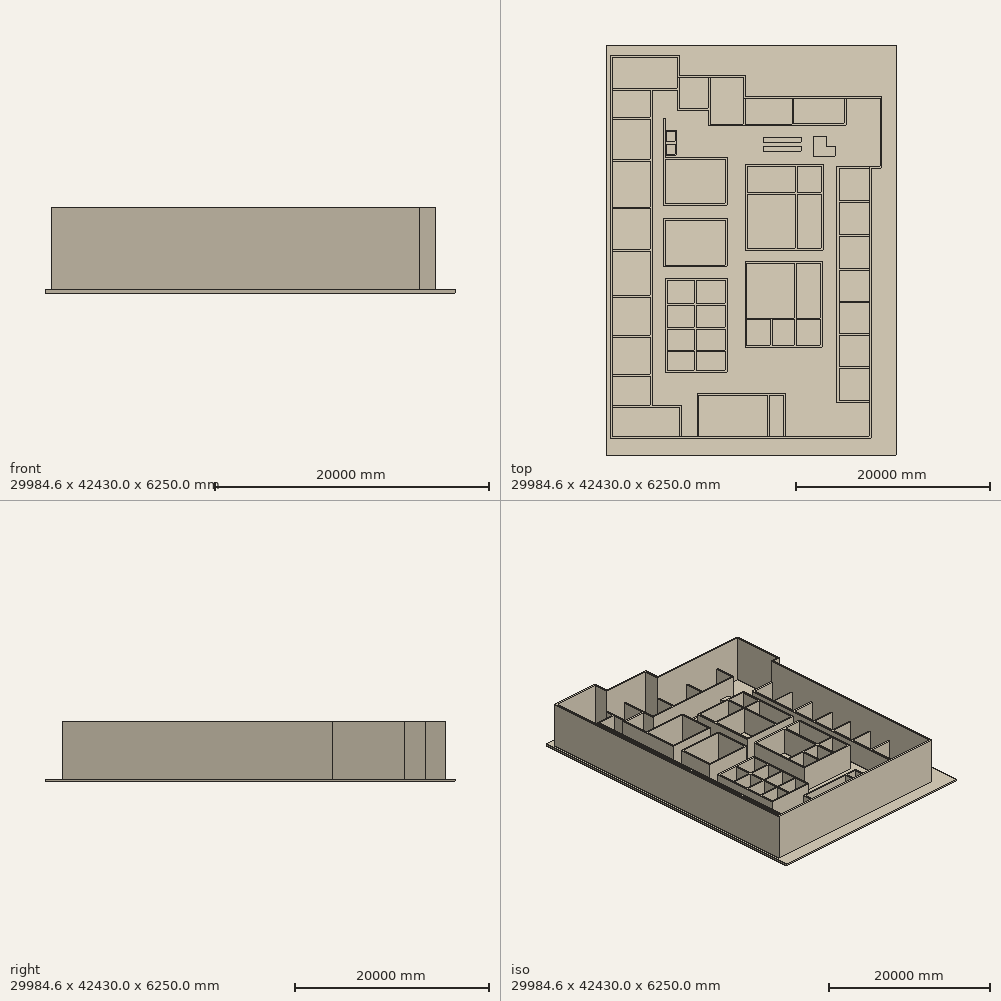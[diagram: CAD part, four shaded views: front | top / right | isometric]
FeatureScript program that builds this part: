
annotation { "Feature Type Name" : "Feature", "Feature Type Description" : "" }
export const myFeature = defineFeature(function(context is Context, id is Id, definition is map)
    precondition{}
    {
        {
            var Q0;
            Q0=qCreatedBy(makeId("Top.planeOp"),FACE);
            var sketch = newSketch(context, id + "F0", { "sketchPlane" : qUnion([Q0])});
            skLineSegment(sketch, "E0", {"start": v(414.42, 1769.53) * mm, "end": v(27384.85, 1769.53) * mm});
            skLineSegment(sketch, "E1", {"start": v(27384.85, 1769.53) * mm, "end": v(27384.85, 29713.26) * mm});
            skLineSegment(sketch, "E2", {"start": v(27384.85, 29713.26) * mm, "end": v(28491.53, 29713.26) * mm});
            skLineSegment(sketch, "E3", {"start": v(28491.53, 29713.26) * mm, "end": v(28491.53, 37144.84) * mm});
            skLineSegment(sketch, "E4", {"start": v(28491.53, 37144.84) * mm, "end": v(14379.1, 37144.84) * mm});
            skLineSegment(sketch, "E5", {"start": v(14379.1, 37144.84) * mm, "end": v(14379.1, 39309.76) * mm});
            skLineSegment(sketch, "E6", {"start": v(14379.1, 39309.76) * mm, "end": v(7514.71, 39309.76) * mm});
            skLineSegment(sketch, "E7", {"start": v(7514.71, 39309.76) * mm, "end": v(7514.71, 41362.76) * mm});
            skLineSegment(sketch, "E8", {"start": v(7514.71, 41362.76) * mm, "end": v(414.42, 41362.76) * mm});
            skLineSegment(sketch, "E9", {"start": v(414.42, 41362.76) * mm, "end": v(414.42, 1769.53) * mm});
            skLineSegment(sketch, "E10", {"start": v(614.42, 1969.53) * mm, "end": v(27184.85, 1969.53) * mm});
            skLineSegment(sketch, "E11", {"start": v(27184.85, 1969.53) * mm, "end": v(27184.85, 29913.26) * mm});
            skLineSegment(sketch, "E12", {"start": v(27184.85, 29913.26) * mm, "end": v(28291.53, 29913.26) * mm});
            skLineSegment(sketch, "E13", {"start": v(28291.53, 29913.26) * mm, "end": v(28291.53, 36944.84) * mm});
            skLineSegment(sketch, "E14", {"start": v(28291.53, 36944.84) * mm, "end": v(14179.1, 36944.84) * mm});
            skLineSegment(sketch, "E15", {"start": v(14179.1, 36944.84) * mm, "end": v(14179.1, 39109.76) * mm});
            skLineSegment(sketch, "E16", {"start": v(14179.1, 39109.76) * mm, "end": v(7314.71, 39109.76) * mm});
            skLineSegment(sketch, "E17", {"start": v(7314.71, 39109.76) * mm, "end": v(7314.71, 41162.76) * mm});
            skLineSegment(sketch, "E18", {"start": v(7314.71, 41162.76) * mm, "end": v(614.42, 41162.76) * mm});
            skLineSegment(sketch, "E19", {"start": v(614.42, 41162.76) * mm, "end": v(614.42, 1969.53) * mm});
            skSolve(sketch);
        }
        {
            var Q0;
            Q0=makeQuery(id+"F0.imprint","IMPRINT",FACE,{"disambiguationData":[TD([[makeQuery(id+"F0.imprint","IMPRINT",EDGE,{"derivedFrom":sQuery(id+"F0.wireOp",EDGE,"E0")}),1.0]])]});
            extrude(context, id + "F1", {"entities" : qUnion([Q0]), "depth" : 6000 * mm, "offsetDistance" : 25 * mm});
        }
        {
            var Q0;
            Q0=qCreatedBy(makeId("Top.planeOp"),FACE);
            var sketch = newSketch(context, id + "F2", { "sketchPlane" : qUnion([Q0])});
            skLineSegment(sketch, "E20.bottom", {"start": v(18534.6, 6431.3) * mm, "end": v(9367.4, 6431.3) * mm});
            skLineSegment(sketch, "E20.top", {"start": v(18534.6, 1969.52) * mm, "end": v(9367.4, 1969.52) * mm});
            skLineSegment(sketch, "E20.left", {"start": v(18534.6, 6431.3) * mm, "end": v(18534.6, 1969.52) * mm});
            skLineSegment(sketch, "E20.right", {"start": v(9367.4, 6431.3) * mm, "end": v(9367.4, 1969.52) * mm});
            skLineSegment(sketch, "E21.bottom", {"start": v(9542.41, 6224.02) * mm, "end": v(16684.38, 6224.02) * mm});
            skLineSegment(sketch, "E21.top", {"start": v(9542.41, 1969.52) * mm, "end": v(16684.38, 1969.52) * mm});
            skLineSegment(sketch, "E21.left", {"start": v(9542.41, 6224.02) * mm, "end": v(9542.41, 1969.52) * mm});
            skLineSegment(sketch, "E21.right", {"start": v(16684.38, 6224.02) * mm, "end": v(16684.38, 1969.52) * mm});
            skLineSegment(sketch, "E22.bottom", {"start": v(16877.72, 6224.02) * mm, "end": v(18340.36, 6224.02) * mm});
            skLineSegment(sketch, "E22.top", {"start": v(16877.72, 1969.52) * mm, "end": v(18340.36, 1969.52) * mm});
            skLineSegment(sketch, "E22.left", {"start": v(16877.72, 6224.02) * mm, "end": v(16877.72, 1969.52) * mm});
            skLineSegment(sketch, "E22.right", {"start": v(18340.36, 6224.02) * mm, "end": v(18340.36, 1969.52) * mm});
            skSolve(sketch);
        }
        {
            var Q0;
            Q0=makeQuery(id+"F2.imprint","IMPRINT",FACE,{"disambiguationData":[TD([[makeQuery(id+"F2.imprint","IMPRINT",EDGE,{"derivedFrom":sQuery(id+"F2.wireOp",EDGE,"E20.bottom")}),1.0]])]});
            extrude(context, id + "F3", {"entities" : qUnion([Q0]), "depth" : 3500 * mm, "offsetDistance" : 25 * mm});
        }
        {
            var Q0;
            Q0=qCreatedBy(makeId("Top.planeOp"),FACE);
            var sketch = newSketch(context, id + "F4", { "sketchPlane" : qUnion([Q0])});
            skLineSegment(sketch, "E23.bottom", {"start": v(7784.5, 1967.61) * mm, "end": v(609.72, 1967.61) * mm});
            skLineSegment(sketch, "E23.top", {"start": v(7784.5, 5141.6) * mm, "end": v(609.72, 5141.6) * mm});
            skLineSegment(sketch, "E23.left", {"start": v(7784.5, 1967.61) * mm, "end": v(7784.5, 5141.6) * mm});
            skLineSegment(sketch, "E23.right", {"start": v(609.72, 1967.61) * mm, "end": v(609.72, 5141.6) * mm});
            skLineSegment(sketch, "E24.bottom", {"start": v(609.72, 4967.2) * mm, "end": v(7570.65, 4967.2) * mm});
            skLineSegment(sketch, "E24.top", {"start": v(609.72, 1967.61) * mm, "end": v(7570.65, 1967.61) * mm});
            skLineSegment(sketch, "E24.left", {"start": v(609.72, 4967.2) * mm, "end": v(609.72, 1967.61) * mm});
            skLineSegment(sketch, "E24.right", {"start": v(7570.65, 4967.2) * mm, "end": v(7570.65, 1967.61) * mm});
            skLineSegment(sketch, "E25.bottom", {"start": v(4738.63, 5141.6) * mm, "end": v(609.72, 5141.6) * mm});
            skLineSegment(sketch, "E25.top", {"start": v(4738.63, 8338.8) * mm, "end": v(609.72, 8338.8) * mm});
            skLineSegment(sketch, "E25.left", {"start": v(4738.63, 5141.6) * mm, "end": v(4738.63, 8338.8) * mm});
            skLineSegment(sketch, "E25.right", {"start": v(609.72, 5141.6) * mm, "end": v(609.72, 8338.8) * mm});
            skLineSegment(sketch, "E26.bottom", {"start": v(609.72, 8160.97) * mm, "end": v(4559, 8160.97) * mm});
            skLineSegment(sketch, "E26.top", {"start": v(609.72, 5141.6) * mm, "end": v(4559, 5141.6) * mm});
            skLineSegment(sketch, "E26.left", {"start": v(609.72, 8160.97) * mm, "end": v(609.72, 5141.6) * mm});
            skLineSegment(sketch, "E26.right", {"start": v(4559, 8160.97) * mm, "end": v(4559, 5141.6) * mm});
            skLineSegment(sketch, "E27.top", {"start": v(4738.63, 12384.25) * mm, "end": v(609.72, 12384.25) * mm});
            skLineSegment(sketch, "E27.left", {"start": v(4738.63, 8338.8) * mm, "end": v(4738.63, 12384.25) * mm});
            skLineSegment(sketch, "E27.right", {"start": v(609.72, 8338.8) * mm, "end": v(609.72, 12384.25) * mm});
            skLineSegment(sketch, "E28.bottom", {"start": v(609.72, 12225.64) * mm, "end": v(4559, 12225.64) * mm});
            skLineSegment(sketch, "E28.top", {"start": v(609.72, 8338.8) * mm, "end": v(4559, 8338.8) * mm});
            skLineSegment(sketch, "E28.left", {"start": v(609.72, 12225.64) * mm, "end": v(609.72, 8338.8) * mm});
            skLineSegment(sketch, "E28.right", {"start": v(4559, 12225.64) * mm, "end": v(4559, 8338.8) * mm});
            skLineSegment(sketch, "E29.top", {"start": v(4738.63, 16526.3) * mm, "end": v(609.72, 16526.3) * mm});
            skLineSegment(sketch, "E29.left", {"start": v(4738.63, 12384.25) * mm, "end": v(4738.63, 16526.3) * mm});
            skLineSegment(sketch, "E29.right", {"start": v(609.72, 12384.25) * mm, "end": v(609.72, 16526.3) * mm});
            skLineSegment(sketch, "E30.bottom", {"start": v(609.72, 16367) * mm, "end": v(4559, 16367) * mm});
            skLineSegment(sketch, "E30.top", {"start": v(609.72, 12384.25) * mm, "end": v(4559, 12384.25) * mm});
            skLineSegment(sketch, "E30.left", {"start": v(609.72, 16367) * mm, "end": v(609.72, 12384.25) * mm});
            skLineSegment(sketch, "E30.right", {"start": v(4559, 16367) * mm, "end": v(4559, 12384.25) * mm});
            skLineSegment(sketch, "E31.top", {"start": v(4738.63, 21320.6) * mm, "end": v(609.72, 21320.6) * mm});
            skLineSegment(sketch, "E31.left", {"start": v(4738.63, 16526.3) * mm, "end": v(4738.63, 21320.6) * mm});
            skLineSegment(sketch, "E31.right", {"start": v(609.72, 16526.3) * mm, "end": v(609.72, 21320.6) * mm});
            skLineSegment(sketch, "E32.bottom", {"start": v(609.72, 21131.98) * mm, "end": v(4559, 21131.98) * mm});
            skLineSegment(sketch, "E32.top", {"start": v(609.72, 16526.3) * mm, "end": v(4559, 16526.3) * mm});
            skLineSegment(sketch, "E32.left", {"start": v(609.72, 21131.98) * mm, "end": v(609.72, 16526.3) * mm});
            skLineSegment(sketch, "E32.right", {"start": v(4559, 21131.98) * mm, "end": v(4559, 16526.3) * mm});
            skLineSegment(sketch, "E33.top", {"start": v(4738.63, 25696.66) * mm, "end": v(609.72, 25696.66) * mm});
            skLineSegment(sketch, "E33.left", {"start": v(4738.63, 21320.6) * mm, "end": v(4738.63, 25696.66) * mm});
            skLineSegment(sketch, "E33.right", {"start": v(609.72, 21320.6) * mm, "end": v(609.72, 25696.66) * mm});
            skLineSegment(sketch, "E34.bottom", {"start": v(609.72, 25533.64) * mm, "end": v(4559, 25533.64) * mm});
            skLineSegment(sketch, "E34.top", {"start": v(609.72, 21320.6) * mm, "end": v(4559, 21320.6) * mm});
            skLineSegment(sketch, "E34.left", {"start": v(609.72, 25533.64) * mm, "end": v(609.72, 21320.6) * mm});
            skLineSegment(sketch, "E34.right", {"start": v(4559, 25533.64) * mm, "end": v(4559, 21320.6) * mm});
            skLineSegment(sketch, "E35.top", {"start": v(4738.63, 30588.27) * mm, "end": v(609.72, 30588.27) * mm});
            skLineSegment(sketch, "E35.left", {"start": v(4738.63, 25696.66) * mm, "end": v(4738.63, 30588.27) * mm});
            skLineSegment(sketch, "E35.right", {"start": v(609.72, 25696.66) * mm, "end": v(609.72, 30588.27) * mm});
            skLineSegment(sketch, "E36.bottom", {"start": v(609.72, 30407.33) * mm, "end": v(4559, 30407.33) * mm});
            skLineSegment(sketch, "E36.top", {"start": v(609.72, 25696.66) * mm, "end": v(4559, 25696.66) * mm});
            skLineSegment(sketch, "E36.left", {"start": v(609.72, 30407.33) * mm, "end": v(609.72, 25696.66) * mm});
            skLineSegment(sketch, "E36.right", {"start": v(4559, 30407.33) * mm, "end": v(4559, 25696.66) * mm});
            skLineSegment(sketch, "E37.top", {"start": v(4738.63, 34934.96) * mm, "end": v(609.72, 34934.96) * mm});
            skLineSegment(sketch, "E37.left", {"start": v(4738.63, 30588.27) * mm, "end": v(4738.63, 34934.96) * mm});
            skLineSegment(sketch, "E37.right", {"start": v(609.72, 30588.27) * mm, "end": v(609.72, 34934.96) * mm});
            skLineSegment(sketch, "E38.bottom", {"start": v(609.72, 34776.35) * mm, "end": v(4559, 34776.35) * mm});
            skLineSegment(sketch, "E38.top", {"start": v(609.72, 30588.27) * mm, "end": v(4559, 30588.27) * mm});
            skLineSegment(sketch, "E38.left", {"start": v(609.72, 34776.35) * mm, "end": v(609.72, 30588.27) * mm});
            skLineSegment(sketch, "E38.right", {"start": v(4559, 34776.35) * mm, "end": v(4559, 30588.27) * mm});
            skLineSegment(sketch, "E39.top", {"start": v(4738.63, 37981.85) * mm, "end": v(609.72, 37981.85) * mm});
            skLineSegment(sketch, "E39.left", {"start": v(4738.63, 34934.96) * mm, "end": v(4738.63, 37981.85) * mm});
            skLineSegment(sketch, "E39.right", {"start": v(609.72, 34934.96) * mm, "end": v(609.72, 37981.85) * mm});
            skLineSegment(sketch, "E40.bottom", {"start": v(609.72, 37824.67) * mm, "end": v(4559, 37824.67) * mm});
            skLineSegment(sketch, "E40.top", {"start": v(609.72, 34934.96) * mm, "end": v(4559, 34934.96) * mm});
            skLineSegment(sketch, "E40.left", {"start": v(609.72, 37824.67) * mm, "end": v(609.72, 34934.96) * mm});
            skLineSegment(sketch, "E40.right", {"start": v(4559, 37824.67) * mm, "end": v(4559, 34934.96) * mm});
            skSolve(sketch);
        }
        {
            var Q0;
            {var subQ3=sQuery(id+"F4.wireOp",EDGE,"E23.left");Q0=makeQuery(id+"F4.imprint","IMPRINT",FACE,{"disambiguationData":[TD([[makeQuery(id+"F4.imprint","IMPRINT",EDGE,{"derivedFrom":subQ3}),1.0]])]});}
            var Q1;
            {var subQ0=sQuery(id+"F4.wireOp",EDGE,"E25.left");Q1=makeQuery(id+"F4.imprint","IMPRINT",FACE,{"disambiguationData":[TD([[makeQuery(id+"F4.imprint","IMPRINT",EDGE,{"derivedFrom":subQ0}),1.0]])]});}
            var Q2;
            {var subQ0=sQuery(id+"F4.wireOp",EDGE,"E27.left");Q2=makeQuery(id+"F4.imprint","IMPRINT",FACE,{"disambiguationData":[TD([[makeQuery(id+"F4.imprint","IMPRINT",EDGE,{"derivedFrom":subQ0}),1.0]])]});}
            var Q3;
            {var subQ0=sQuery(id+"F4.wireOp",EDGE,"E29.left");Q3=makeQuery(id+"F4.imprint","IMPRINT",FACE,{"disambiguationData":[TD([[makeQuery(id+"F4.imprint","IMPRINT",EDGE,{"derivedFrom":subQ0}),1.0]])]});}
            var Q4;
            {var subQ0=sQuery(id+"F4.wireOp",EDGE,"E31.left");Q4=makeQuery(id+"F4.imprint","IMPRINT",FACE,{"disambiguationData":[TD([[makeQuery(id+"F4.imprint","IMPRINT",EDGE,{"derivedFrom":subQ0}),1.0]])]});}
            var Q5;
            {var subQ0=sQuery(id+"F4.wireOp",EDGE,"E33.left");Q5=makeQuery(id+"F4.imprint","IMPRINT",FACE,{"disambiguationData":[TD([[makeQuery(id+"F4.imprint","IMPRINT",EDGE,{"derivedFrom":subQ0}),1.0]])]});}
            var Q6;
            {var subQ0=sQuery(id+"F4.wireOp",EDGE,"E35.left");Q6=makeQuery(id+"F4.imprint","IMPRINT",FACE,{"disambiguationData":[TD([[makeQuery(id+"F4.imprint","IMPRINT",EDGE,{"derivedFrom":subQ0}),1.0]])]});}
            var Q7;
            {var subQ0=sQuery(id+"F4.wireOp",EDGE,"E37.left");Q7=makeQuery(id+"F4.imprint","IMPRINT",FACE,{"disambiguationData":[TD([[makeQuery(id+"F4.imprint","IMPRINT",EDGE,{"derivedFrom":subQ0}),1.0]])]});}
            var Q8;
            {var subQ1=sQuery(id+"F4.wireOp",EDGE,"E39.top");Q8=makeQuery(id+"F4.imprint","IMPRINT",FACE,{"disambiguationData":[TD([[makeQuery(id+"F4.imprint","IMPRINT",EDGE,{"derivedFrom":subQ1}),1.0]])]});}
            extrude(context, id + "F5", {"entities" : qUnion([Q0, Q1, Q2, Q3, Q4, Q5, Q6, Q7, Q8]), "depth" : 3000 * mm, "offsetDistance" : 25 * mm});
        }
        {
            var Q0;
            Q0=qCreatedBy(makeId("Top.planeOp"),FACE);
            var sketch = newSketch(context, id + "F6", { "sketchPlane" : qUnion([Q0])});
            skLineSegment(sketch, "E41.bottom", {"start": v(24779.92, 36969.18) * mm, "end": v(19212.86, 36969.18) * mm});
            skLineSegment(sketch, "E41.top", {"start": v(24779.92, 34117.8) * mm, "end": v(19212.86, 34117.8) * mm});
            skLineSegment(sketch, "E41.left", {"start": v(24779.92, 36969.18) * mm, "end": v(24779.92, 34117.8) * mm});
            skLineSegment(sketch, "E41.right", {"start": v(19212.86, 36969.18) * mm, "end": v(19212.86, 34117.8) * mm});
            skLineSegment(sketch, "E42.bottom", {"start": v(19389.23, 34324.37) * mm, "end": v(24610.44, 34324.37) * mm});
            skLineSegment(sketch, "E42.top", {"start": v(19389.23, 36969.18) * mm, "end": v(24610.44, 36969.18) * mm});
            skLineSegment(sketch, "E42.left", {"start": v(19389.23, 34324.37) * mm, "end": v(19389.23, 36969.18) * mm});
            skLineSegment(sketch, "E42.right", {"start": v(24610.44, 34324.37) * mm, "end": v(24610.44, 36969.18) * mm});
            skLineSegment(sketch, "E43", {"start": v(19212.86, 36969.18) * mm, "end": v(13851.37, 36969.18) * mm, "construction": true});
            skLineSegment(sketch, "E44", {"start": v(14179.1, 36969.18) * mm, "end": v(14179.1, 34117.8) * mm, "construction": true});
            skLineSegment(sketch, "E45.bottom", {"start": v(14179.1, 36969.18) * mm, "end": v(19212.86, 36969.18) * mm});
            skLineSegment(sketch, "E45.top", {"start": v(14179.1, 34117.8) * mm, "end": v(19212.86, 34117.8) * mm});
            skLineSegment(sketch, "E45.left", {"start": v(14179.1, 36969.18) * mm, "end": v(14179.1, 34117.8) * mm});
            skLineSegment(sketch, "E46.bottom", {"start": v(19212.86, 34295.57) * mm, "end": v(14365.95, 34295.57) * mm});
            skLineSegment(sketch, "E46.top", {"start": v(19212.86, 36969.18) * mm, "end": v(14365.95, 36969.18) * mm});
            skLineSegment(sketch, "E46.left", {"start": v(19212.86, 34295.57) * mm, "end": v(19212.86, 36969.18) * mm});
            skLineSegment(sketch, "E46.right", {"start": v(14365.95, 34295.57) * mm, "end": v(14365.95, 36969.18) * mm});
            skLineSegment(sketch, "E47.bottom", {"start": v(14179.1, 34117.8) * mm, "end": v(10513.24, 34117.8) * mm});
            skLineSegment(sketch, "E47.top", {"start": v(14179.1, 39118.15) * mm, "end": v(10513.24, 39118.15) * mm});
            skLineSegment(sketch, "E47.left", {"start": v(14179.1, 34117.8) * mm, "end": v(14179.1, 39118.15) * mm});
            skLineSegment(sketch, "E47.right", {"start": v(10513.24, 34117.8) * mm, "end": v(10513.24, 39118.15) * mm});
            skLineSegment(sketch, "E48.bottom", {"start": v(14179.1, 34295.57) * mm, "end": v(10708.2, 34295.57) * mm});
            skLineSegment(sketch, "E48.top", {"start": v(14179.1, 39118.15) * mm, "end": v(10708.2, 39118.15) * mm});
            skLineSegment(sketch, "E48.left", {"start": v(14179.1, 34295.57) * mm, "end": v(14179.1, 39118.15) * mm});
            skLineSegment(sketch, "E48.right", {"start": v(10708.2, 34295.57) * mm, "end": v(10708.2, 39118.15) * mm});
            skLineSegment(sketch, "E49.bottom", {"start": v(10513.24, 35728.09) * mm, "end": v(7321.54, 35728.09) * mm});
            skLineSegment(sketch, "E49.top", {"start": v(10513.24, 39118.15) * mm, "end": v(7321.54, 39118.15) * mm});
            skLineSegment(sketch, "E49.left", {"start": v(10513.24, 35728.09) * mm, "end": v(10513.24, 39118.15) * mm});
            skLineSegment(sketch, "E49.right", {"start": v(7321.54, 35728.09) * mm, "end": v(7321.54, 39118.15) * mm});
            skLineSegment(sketch, "E50.bottom", {"start": v(10513.24, 35943.79) * mm, "end": v(7494.73, 35943.79) * mm});
            skLineSegment(sketch, "E50.top", {"start": v(10513.24, 39118.15) * mm, "end": v(7494.73, 39118.15) * mm});
            skLineSegment(sketch, "E50.left", {"start": v(10513.24, 35943.79) * mm, "end": v(10513.24, 39118.15) * mm});
            skLineSegment(sketch, "E50.right", {"start": v(7494.73, 35943.79) * mm, "end": v(7494.73, 39118.15) * mm});
            skLineSegment(sketch, "E51.bottom", {"start": v(4723.43, 37978.8) * mm, "end": v(7321.54, 37978.8) * mm});
            skLineSegment(sketch, "E51.top", {"start": v(4723.43, 37815.59) * mm, "end": v(7321.54, 37815.59) * mm});
            skLineSegment(sketch, "E51.left", {"start": v(4723.43, 37978.8) * mm, "end": v(4723.43, 37815.59) * mm});
            skLineSegment(sketch, "E51.right", {"start": v(7321.54, 37978.8) * mm, "end": v(7321.54, 37815.59) * mm});
            skSolve(sketch);
        }
        {
            var Q0;
            {var subQ0=sQuery(id+"F6.wireOp",EDGE,"E51.bottom");Q0=makeQuery(id+"F6.imprint","IMPRINT",FACE,{"disambiguationData":[TD([[makeQuery(id+"F6.imprint","IMPRINT",EDGE,{"derivedFrom":subQ0}),-1.0]])]});}
            var Q1;
            {var subQ1=sQuery(id+"F6.wireOp",EDGE,"E49.bottom");Q1=makeQuery(id+"F6.imprint","IMPRINT",FACE,{"disambiguationData":[TD([[makeQuery(id+"F6.imprint","IMPRINT",EDGE,{"derivedFrom":subQ1}),-1.0]])]});}
            var Q2;
            {var subQ4=sQuery(id+"F6.wireOp",EDGE,"E47.bottom");Q2=makeQuery(id+"F6.imprint","IMPRINT",FACE,{"disambiguationData":[TD([[makeQuery(id+"F6.imprint","IMPRINT",EDGE,{"derivedFrom":subQ4}),-1.0]])]});}
            var Q3;
            {var subQ4=sQuery(id+"F6.wireOp",EDGE,"E45.top");Q3=makeQuery(id+"F6.imprint","IMPRINT",FACE,{"disambiguationData":[TD([[makeQuery(id+"F6.imprint","IMPRINT",EDGE,{"derivedFrom":subQ4}),1.0]])]});}
            var Q4;
            {var subQ1=sQuery(id+"F6.wireOp",EDGE,"E41.top");Q4=makeQuery(id+"F6.imprint","IMPRINT",FACE,{"disambiguationData":[TD([[makeQuery(id+"F6.imprint","IMPRINT",EDGE,{"derivedFrom":subQ1}),-1.0]])]});}
            extrude(context, id + "F7", {"entities" : qUnion([Q0, Q1, Q2, Q3, Q4]), "depth" : 3000 * mm, "offsetDistance" : 25 * mm});
        }
        {
            var Q0;
            Q0=qCreatedBy(makeId("Top.planeOp"),FACE);
            var sketch = newSketch(context, id + "F8", { "sketchPlane" : qUnion([Q0])});
            skLineSegment(sketch, "E52.bottom", {"start": v(27206.14, 5463.2) * mm, "end": v(23827.33, 5463.2) * mm});
            skLineSegment(sketch, "E52.top", {"start": v(27206.14, 29937.1) * mm, "end": v(23827.33, 29937.1) * mm});
            skLineSegment(sketch, "E52.left", {"start": v(27206.14, 5463.2) * mm, "end": v(27206.14, 29937.1) * mm});
            skLineSegment(sketch, "E52.right", {"start": v(23827.33, 5463.2) * mm, "end": v(23827.33, 29937.1) * mm});
            skLineSegment(sketch, "E53.bottom", {"start": v(24058.5, 29721.69) * mm, "end": v(27206.14, 29721.69) * mm});
            skLineSegment(sketch, "E53.top", {"start": v(24058.5, 26383.7) * mm, "end": v(27206.14, 26383.7) * mm});
            skLineSegment(sketch, "E53.left", {"start": v(24058.5, 29721.69) * mm, "end": v(24058.5, 26383.7) * mm});
            skLineSegment(sketch, "E53.right", {"start": v(27206.14, 29721.69) * mm, "end": v(27206.14, 26383.7) * mm});
            skLineSegment(sketch, "E54.bottom", {"start": v(24058.5, 26211.66) * mm, "end": v(27206.14, 26211.66) * mm});
            skLineSegment(sketch, "E54.top", {"start": v(24058.5, 22860.98) * mm, "end": v(27206.14, 22860.98) * mm});
            skLineSegment(sketch, "E54.left", {"start": v(24058.5, 26211.66) * mm, "end": v(24058.5, 22860.98) * mm});
            skLineSegment(sketch, "E54.right", {"start": v(27206.14, 26211.66) * mm, "end": v(27206.14, 22860.98) * mm});
            skLineSegment(sketch, "E55.bottom", {"start": v(24058.5, 22674.67) * mm, "end": v(27206.14, 22674.67) * mm});
            skLineSegment(sketch, "E55.top", {"start": v(24058.5, 19320.51) * mm, "end": v(27206.14, 19320.51) * mm});
            skLineSegment(sketch, "E55.left", {"start": v(24058.5, 22674.67) * mm, "end": v(24058.5, 19320.51) * mm});
            skLineSegment(sketch, "E55.right", {"start": v(27206.14, 22674.67) * mm, "end": v(27206.14, 19320.51) * mm});
            skLineSegment(sketch, "E56.bottom", {"start": v(24058.5, 19131.43) * mm, "end": v(27206.14, 19131.43) * mm});
            skLineSegment(sketch, "E56.top", {"start": v(24058.5, 15983.74) * mm, "end": v(27206.14, 15983.74) * mm});
            skLineSegment(sketch, "E56.left", {"start": v(24058.5, 19131.43) * mm, "end": v(24058.5, 15983.74) * mm});
            skLineSegment(sketch, "E56.right", {"start": v(27206.14, 19131.43) * mm, "end": v(27206.14, 15983.74) * mm});
            skLineSegment(sketch, "E57.bottom", {"start": v(24058.5, 15843.81) * mm, "end": v(27206.14, 15843.81) * mm});
            skLineSegment(sketch, "E57.top", {"start": v(24058.5, 12593.1) * mm, "end": v(27206.14, 12593.1) * mm});
            skLineSegment(sketch, "E57.left", {"start": v(24058.5, 15843.81) * mm, "end": v(24058.5, 12593.1) * mm});
            skLineSegment(sketch, "E57.right", {"start": v(27206.14, 15843.81) * mm, "end": v(27206.14, 12593.1) * mm});
            skLineSegment(sketch, "E58.bottom", {"start": v(24058.5, 12385.82) * mm, "end": v(27206.14, 12385.82) * mm});
            skLineSegment(sketch, "E58.top", {"start": v(24058.5, 9177.79) * mm, "end": v(27206.14, 9177.79) * mm});
            skLineSegment(sketch, "E58.left", {"start": v(24058.5, 12385.82) * mm, "end": v(24058.5, 9177.79) * mm});
            skLineSegment(sketch, "E58.right", {"start": v(27206.14, 12385.82) * mm, "end": v(27206.14, 9177.79) * mm});
            skLineSegment(sketch, "E59.bottom", {"start": v(24058.5, 8973.56) * mm, "end": v(27206.14, 8973.56) * mm});
            skLineSegment(sketch, "E59.top", {"start": v(24058.5, 5658.96) * mm, "end": v(27206.14, 5658.96) * mm});
            skLineSegment(sketch, "E59.left", {"start": v(24058.5, 8973.56) * mm, "end": v(24058.5, 5658.96) * mm});
            skLineSegment(sketch, "E59.right", {"start": v(27206.14, 8973.56) * mm, "end": v(27206.14, 5658.96) * mm});
            skSolve(sketch);
        }
        {
            var Q0;
            {var subQ10=sQuery(id+"F8.wireOp",EDGE,"E52.bottom");Q0=makeQuery(id+"F8.imprint","IMPRINT",FACE,{"disambiguationData":[TD([[makeQuery(id+"F8.imprint","IMPRINT",EDGE,{"derivedFrom":subQ10}),-1.0]])]});}
            extrude(context, id + "F9", {"entities" : qUnion([Q0]), "depth" : 3000 * mm, "offsetDistance" : 25 * mm});
        }
        {
            var Q0;
            Q0=qCreatedBy(makeId("Top.planeOp"),FACE);
            var sketch = newSketch(context, id + "F10", { "sketchPlane" : qUnion([Q0])});
            skLineSegment(sketch, "E60.bottom", {"start": v(6065.93, 18287.14) * mm, "end": v(12485.88, 18287.14) * mm});
            skLineSegment(sketch, "E60.top", {"start": v(6065.93, 8587.14) * mm, "end": v(12485.88, 8587.14) * mm});
            skLineSegment(sketch, "E60.left", {"start": v(6065.93, 18287.14) * mm, "end": v(6065.93, 8587.14) * mm});
            skLineSegment(sketch, "E60.right", {"start": v(12485.88, 18287.14) * mm, "end": v(12485.88, 8587.14) * mm});
            skLineSegment(sketch, "E61.bottom", {"start": v(9118.23, 8587.14) * mm, "end": v(6270.17, 8587.14) * mm});
            skLineSegment(sketch, "E61.top", {"start": v(9118.23, 18075.79) * mm, "end": v(6270.17, 18075.79) * mm});
            skLineSegment(sketch, "E61.left", {"start": v(9118.23, 8587.14) * mm, "end": v(9118.23, 18075.79) * mm});
            skLineSegment(sketch, "E61.right", {"start": v(6270.17, 8587.14) * mm, "end": v(6270.17, 18075.79) * mm});
            skLineSegment(sketch, "E62.bottom", {"start": v(9275.9, 8587.14) * mm, "end": v(12314.9, 8587.14) * mm});
            skLineSegment(sketch, "E62.top", {"start": v(9275.9, 18075.79) * mm, "end": v(12314.9, 18075.79) * mm});
            skLineSegment(sketch, "E62.left", {"start": v(9275.9, 8587.14) * mm, "end": v(9275.9, 18075.79) * mm});
            skLineSegment(sketch, "E62.right", {"start": v(12314.9, 8587.14) * mm, "end": v(12314.9, 18075.79) * mm});
            skLineSegment(sketch, "E63.bottom", {"start": v(9118.23, 8784.3) * mm, "end": v(6270.17, 8784.3) * mm});
            skLineSegment(sketch, "E63.top", {"start": v(9118.23, 10747.02) * mm, "end": v(6270.17, 10747.02) * mm});
            skLineSegment(sketch, "E63.left", {"start": v(9118.23, 8784.3) * mm, "end": v(9118.23, 10747.02) * mm});
            skLineSegment(sketch, "E63.right", {"start": v(6270.17, 8784.3) * mm, "end": v(6270.17, 10747.02) * mm});
            skLineSegment(sketch, "E64.bottom", {"start": v(9118.23, 10888.08) * mm, "end": v(6270.17, 10888.08) * mm});
            skLineSegment(sketch, "E64.top", {"start": v(9118.23, 13086.93) * mm, "end": v(6270.17, 13086.93) * mm});
            skLineSegment(sketch, "E64.left", {"start": v(9118.23, 10888.08) * mm, "end": v(9118.23, 13086.93) * mm});
            skLineSegment(sketch, "E64.right", {"start": v(6270.17, 10888.08) * mm, "end": v(6270.17, 13086.93) * mm});
            skLineSegment(sketch, "E65.bottom", {"start": v(9118.23, 13242.14) * mm, "end": v(6270.17, 13242.14) * mm});
            skLineSegment(sketch, "E65.top", {"start": v(9118.23, 15491.96) * mm, "end": v(6270.17, 15491.96) * mm});
            skLineSegment(sketch, "E65.left", {"start": v(9118.23, 13242.14) * mm, "end": v(9118.23, 15491.96) * mm});
            skLineSegment(sketch, "E65.right", {"start": v(6270.17, 13242.14) * mm, "end": v(6270.17, 15491.96) * mm});
            skLineSegment(sketch, "E66.bottom", {"start": v(9118.23, 15682.93) * mm, "end": v(6270.17, 15682.93) * mm});
            skLineSegment(sketch, "E66.left", {"start": v(9118.23, 15682.93) * mm, "end": v(9118.23, 18075.79) * mm});
            skLineSegment(sketch, "E66.right", {"start": v(6270.17, 15682.93) * mm, "end": v(6270.17, 18075.79) * mm});
            skLineSegment(sketch, "E67.bottom", {"start": v(9275.9, 15682.93) * mm, "end": v(12314.9, 15682.93) * mm});
            skLineSegment(sketch, "E67.left", {"start": v(9275.9, 15682.93) * mm, "end": v(9275.9, 18075.79) * mm});
            skLineSegment(sketch, "E67.right", {"start": v(12314.9, 15682.93) * mm, "end": v(12314.9, 18075.79) * mm});
            skLineSegment(sketch, "E68.bottom", {"start": v(9275.9, 15491.96) * mm, "end": v(12314.9, 15491.96) * mm});
            skLineSegment(sketch, "E68.top", {"start": v(9275.9, 13242.14) * mm, "end": v(12314.9, 13242.14) * mm});
            skLineSegment(sketch, "E68.left", {"start": v(9275.9, 15491.96) * mm, "end": v(9275.9, 13242.14) * mm});
            skLineSegment(sketch, "E68.right", {"start": v(12314.9, 15491.96) * mm, "end": v(12314.9, 13242.14) * mm});
            skLineSegment(sketch, "E69.bottom", {"start": v(9275.9, 13086.93) * mm, "end": v(12314.9, 13086.93) * mm});
            skLineSegment(sketch, "E69.top", {"start": v(9275.9, 10888.08) * mm, "end": v(12314.9, 10888.08) * mm});
            skLineSegment(sketch, "E69.left", {"start": v(9275.9, 13086.93) * mm, "end": v(9275.9, 10888.08) * mm});
            skLineSegment(sketch, "E69.right", {"start": v(12314.9, 13086.93) * mm, "end": v(12314.9, 10888.08) * mm});
            skLineSegment(sketch, "E70.bottom", {"start": v(9275.9, 10747.02) * mm, "end": v(12314.9, 10747.02) * mm});
            skLineSegment(sketch, "E70.top", {"start": v(9275.9, 8784.3) * mm, "end": v(12314.9, 8784.3) * mm});
            skLineSegment(sketch, "E70.left", {"start": v(9275.9, 10747.02) * mm, "end": v(9275.9, 8784.3) * mm});
            skLineSegment(sketch, "E70.right", {"start": v(12314.9, 10747.02) * mm, "end": v(12314.9, 8784.3) * mm});
            skSolve(sketch);
        }
        {
            var Q0;
            Q0=makeQuery(id+"F10.imprint","IMPRINT",FACE,{"disambiguationData":[TD([[makeQuery(id+"F10.imprint","IMPRINT",EDGE,{"derivedFrom":sQuery(id+"F10.wireOp",EDGE,"E60.bottom")}),-1.0]])]});
            var Q1;
            {var subQ2=sQuery(id+"F10.wireOp",EDGE,"E65.top");Q1=makeQuery(id+"F10.imprint","IMPRINT",FACE,{"disambiguationData":[TD([[makeQuery(id+"F10.imprint","IMPRINT",EDGE,{"derivedFrom":subQ2}),-1.0]])]});}
            var Q2;
            {var subQ0=sQuery(id+"F10.wireOp",EDGE,"E67.bottom");Q2=makeQuery(id+"F10.imprint","IMPRINT",FACE,{"disambiguationData":[TD([[makeQuery(id+"F10.imprint","IMPRINT",EDGE,{"derivedFrom":subQ0}),-1.0]])]});}
            var Q3;
            {var subQ0=sQuery(id+"F10.wireOp",EDGE,"E64.top");Q3=makeQuery(id+"F10.imprint","IMPRINT",FACE,{"disambiguationData":[TD([[makeQuery(id+"F10.imprint","IMPRINT",EDGE,{"derivedFrom":subQ0}),-1.0]])]});}
            var Q4;
            {var subQ0=sQuery(id+"F10.wireOp",EDGE,"E68.top");Q4=makeQuery(id+"F10.imprint","IMPRINT",FACE,{"disambiguationData":[TD([[makeQuery(id+"F10.imprint","IMPRINT",EDGE,{"derivedFrom":subQ0}),-1.0]])]});}
            var Q5;
            {var subQ2=sQuery(id+"F10.wireOp",EDGE,"E63.top");Q5=makeQuery(id+"F10.imprint","IMPRINT",FACE,{"disambiguationData":[TD([[makeQuery(id+"F10.imprint","IMPRINT",EDGE,{"derivedFrom":subQ2}),-1.0]])]});}
            var Q6;
            {var subQ0=sQuery(id+"F10.wireOp",EDGE,"E69.top");Q6=makeQuery(id+"F10.imprint","IMPRINT",FACE,{"disambiguationData":[TD([[makeQuery(id+"F10.imprint","IMPRINT",EDGE,{"derivedFrom":subQ0}),-1.0]])]});}
            var Q7;
            {var subQ5=sQuery(id+"F10.wireOp",EDGE,"E63.bottom");Q7=makeQuery(id+"F10.imprint","IMPRINT",FACE,{"disambiguationData":[TD([[makeQuery(id+"F10.imprint","IMPRINT",EDGE,{"derivedFrom":subQ5}),1.0]])]});}
            var Q8;
            {var subQ5=sQuery(id+"F10.wireOp",EDGE,"E70.top");Q8=makeQuery(id+"F10.imprint","IMPRINT",FACE,{"disambiguationData":[TD([[makeQuery(id+"F10.imprint","IMPRINT",EDGE,{"derivedFrom":subQ5}),-1.0]])]});}
            extrude(context, id + "F11", {"entities" : qUnion([Q0, Q1, Q2, Q3, Q4, Q5, Q6, Q7, Q8]), "depth" : 3000 * mm, "offsetDistance" : 25 * mm});
        }
        {
            var Q0;
            Q0=qCreatedBy(makeId("Top.planeOp"),FACE);
            var sketch = newSketch(context, id + "F12", { "sketchPlane" : qUnion([Q0])});
            skLineSegment(sketch, "E71.bottom", {"start": v(5878.5, 24502.8) * mm, "end": v(12477.83, 24502.8) * mm});
            skLineSegment(sketch, "E71.top", {"start": v(5878.5, 19509.9) * mm, "end": v(12477.83, 19509.9) * mm});
            skLineSegment(sketch, "E71.left", {"start": v(5878.5, 24502.8) * mm, "end": v(5878.5, 19509.9) * mm});
            skLineSegment(sketch, "E71.right", {"start": v(12477.83, 24502.8) * mm, "end": v(12477.83, 19509.9) * mm});
            skLineSegment(sketch, "E72.bottom", {"start": v(6081.87, 24286.47) * mm, "end": v(12312.6, 24286.47) * mm});
            skLineSegment(sketch, "E72.top", {"start": v(6081.87, 19666.42) * mm, "end": v(12312.6, 19666.42) * mm});
            skLineSegment(sketch, "E72.left", {"start": v(6081.87, 24286.47) * mm, "end": v(6081.87, 19666.42) * mm});
            skLineSegment(sketch, "E72.right", {"start": v(12312.6, 24286.47) * mm, "end": v(12312.6, 19666.42) * mm});
            skLineSegment(sketch, "E73.bottom", {"start": v(12477.83, 25914.48) * mm, "end": v(5878.5, 25914.48) * mm});
            skLineSegment(sketch, "E73.top", {"start": v(12477.83, 30825.61) * mm, "end": v(5878.5, 30825.61) * mm});
            skLineSegment(sketch, "E73.left", {"start": v(12477.83, 25914.48) * mm, "end": v(12477.83, 30825.61) * mm});
            skLineSegment(sketch, "E73.right", {"start": v(5878.5, 25914.48) * mm, "end": v(5878.5, 30825.61) * mm});
            skLineSegment(sketch, "E74.bottom", {"start": v(6083.35, 30655.19) * mm, "end": v(12309.68, 30655.19) * mm});
            skLineSegment(sketch, "E74.top", {"start": v(6083.35, 26067.09) * mm, "end": v(12309.68, 26067.09) * mm});
            skLineSegment(sketch, "E74.left", {"start": v(6083.35, 30655.19) * mm, "end": v(6083.35, 26067.09) * mm});
            skLineSegment(sketch, "E74.right", {"start": v(12309.68, 30655.19) * mm, "end": v(12309.68, 26067.09) * mm});
            skLineSegment(sketch, "E75.bottom", {"start": v(6083.35, 30825.61) * mm, "end": v(5878.5, 30825.61) * mm});
            skLineSegment(sketch, "E75.top", {"start": v(6083.35, 34915.66) * mm, "end": v(5878.5, 34915.66) * mm});
            skLineSegment(sketch, "E75.left", {"start": v(6083.35, 30825.61) * mm, "end": v(6083.35, 34915.66) * mm});
            skLineSegment(sketch, "E75.right", {"start": v(5878.5, 30825.61) * mm, "end": v(5878.5, 34915.66) * mm});
            skSolve(sketch);
        }
        {
            var Q0;
            Q0=makeQuery(id+"F12.imprint","IMPRINT",FACE,{"disambiguationData":[TD([[makeQuery(id+"F12.imprint","IMPRINT",EDGE,{"derivedFrom":sQuery(id+"F12.wireOp",EDGE,"E71.bottom")}),-1.0]])]});
            var Q1;
            Q1=makeQuery(id+"F12.imprint","IMPRINT",FACE,{"disambiguationData":[TD([[makeQuery(id+"F12.imprint","IMPRINT",EDGE,{"derivedFrom":sQuery(id+"F12.wireOp",EDGE,"E73.bottom")}),-1.0]])]});
            var Q2;
            Q2=makeQuery(id+"F12.imprint","IMPRINT",FACE,{"disambiguationData":[TD([[makeQuery(id+"F12.imprint","IMPRINT",EDGE,{"derivedFrom":sQuery(id+"F12.wireOp",EDGE,"E75.top")}),1.0]])]});
            extrude(context, id + "F13", {"entities" : qUnion([Q0, Q1, Q2]), "depth" : 4000 * mm, "offsetDistance" : 25 * mm});
        }
        {
            var Q0;
            Q0=qCreatedBy(makeId("Top.planeOp"),FACE);
            var sketch = newSketch(context, id + "F14", { "sketchPlane" : qUnion([Q0])});
            skLineSegment(sketch, "E76.bottom", {"start": v(14320.9, 11172.99) * mm, "end": v(22368.6, 11172.99) * mm});
            skLineSegment(sketch, "E76.top", {"start": v(14320.9, 20055.48) * mm, "end": v(22368.6, 20055.48) * mm});
            skLineSegment(sketch, "E76.left", {"start": v(14320.9, 11172.99) * mm, "end": v(14320.9, 20055.48) * mm});
            skLineSegment(sketch, "E76.right", {"start": v(22368.6, 11172.99) * mm, "end": v(22368.6, 20055.48) * mm});
            skLineSegment(sketch, "E77.bottom", {"start": v(14492.62, 19857.79) * mm, "end": v(22170.5, 19857.79) * mm});
            skLineSegment(sketch, "E77.top", {"start": v(14492.62, 11356.62) * mm, "end": v(22170.5, 11356.62) * mm});
            skLineSegment(sketch, "E77.left", {"start": v(14492.62, 19857.79) * mm, "end": v(14492.62, 11356.62) * mm});
            skLineSegment(sketch, "E77.right", {"start": v(22170.5, 19857.79) * mm, "end": v(22170.5, 11356.62) * mm});
            skLineSegment(sketch, "E78.bottom", {"start": v(16938.63, 11356.62) * mm, "end": v(14492.62, 11356.62) * mm});
            skLineSegment(sketch, "E78.top", {"start": v(16938.63, 14036.9) * mm, "end": v(14492.62, 14036.9) * mm});
            skLineSegment(sketch, "E78.left", {"start": v(16938.63, 11356.62) * mm, "end": v(16938.63, 14036.9) * mm});
            skLineSegment(sketch, "E78.right", {"start": v(14492.62, 11356.62) * mm, "end": v(14492.62, 14036.9) * mm});
            skLineSegment(sketch, "E79.bottom", {"start": v(17149.73, 14036.9) * mm, "end": v(19455.11, 14036.9) * mm});
            skLineSegment(sketch, "E79.top", {"start": v(17149.73, 11356.62) * mm, "end": v(19455.11, 11356.62) * mm});
            skLineSegment(sketch, "E79.left", {"start": v(17149.73, 14036.9) * mm, "end": v(17149.73, 11356.62) * mm});
            skLineSegment(sketch, "E79.right", {"start": v(19455.11, 14036.9) * mm, "end": v(19455.11, 11356.62) * mm});
            skLineSegment(sketch, "E80.bottom", {"start": v(19676.23, 14036.9) * mm, "end": v(22170.5, 14036.9) * mm});
            skLineSegment(sketch, "E80.top", {"start": v(19676.23, 11356.62) * mm, "end": v(22170.5, 11356.62) * mm});
            skLineSegment(sketch, "E80.left", {"start": v(19676.23, 14036.9) * mm, "end": v(19676.23, 11356.62) * mm});
            skLineSegment(sketch, "E80.right", {"start": v(22170.5, 14036.9) * mm, "end": v(22170.5, 11356.62) * mm});
            skLineSegment(sketch, "E81.bottom", {"start": v(14320.9, 14209.07) * mm, "end": v(22368.6, 14209.07) * mm});
            skLineSegment(sketch, "E81.top", {"start": v(14320.9, 14036.9) * mm, "end": v(22368.6, 14036.9) * mm});
            skLineSegment(sketch, "E81.left", {"start": v(14320.9, 14209.07) * mm, "end": v(14320.9, 14036.9) * mm});
            skLineSegment(sketch, "E81.right", {"start": v(22368.6, 14209.07) * mm, "end": v(22368.6, 14036.9) * mm});
            skLineSegment(sketch, "E82.bottom", {"start": v(19676.23, 14036.9) * mm, "end": v(19455.11, 14036.9) * mm});
            skLineSegment(sketch, "E82.top", {"start": v(19676.23, 20055.48) * mm, "end": v(19455.11, 20055.48) * mm});
            skLineSegment(sketch, "E82.left", {"start": v(19676.23, 14036.9) * mm, "end": v(19676.23, 20055.48) * mm});
            skLineSegment(sketch, "E82.right", {"start": v(19455.11, 14036.9) * mm, "end": v(19455.11, 20055.48) * mm});
            skSolve(sketch);
        }
        {
            var Q0;
            {var subQ7=sQuery(id+"F14.wireOp",EDGE,"E76.left");var subQ8=sQuery(id+"F14.wireOp",EDGE,"E76.top");var subQ9=makeQuery(id+"F14.imprint","INTERSECT",VERTEX,{"derivedFrom":[subQ8,subQ7]});Q0=makeQuery(id+"F14.imprint","IMPRINT",FACE,{"disambiguationData":[TD([[makeQuery(id+"F14.imprint","IMPRINT",EDGE,{"disambiguationData":[TD([[subQ9,-1.0]])],"derivedFrom":subQ8}),-1.0]])]});}
            var Q1;
            {var subQ5=sQuery(id+"F14.wireOp",EDGE,"E82.left");var subQ9=sQuery(id+"F14.wireOp",EDGE,"E76.top");var subQ11=makeQuery(id+"F14.imprint","INTERSECT",VERTEX,{"derivedFrom":[subQ9,subQ5]});Q1=makeQuery(id+"F14.imprint","IMPRINT",FACE,{"disambiguationData":[TD([[makeQuery(id+"F14.imprint","IMPRINT",EDGE,{"disambiguationData":[TD([[subQ11,-1.0]])],"derivedFrom":subQ9}),-1.0]])]});}
            var Q2;
            {var subQ0=sQuery(id+"F14.wireOp",EDGE,"E82.left");var subQ1=sQuery(id+"F14.wireOp",EDGE,"E76.top");var subQ2=makeQuery(id+"F14.imprint","INTERSECT",VERTEX,{"derivedFrom":[subQ1,subQ0]});Q2=makeQuery(id+"F14.imprint","IMPRINT",FACE,{"disambiguationData":[TD([[makeQuery(id+"F14.imprint","IMPRINT",EDGE,{"disambiguationData":[TD([[subQ2,1.0]])],"derivedFrom":subQ1}),-1.0]])]});}
            var Q3;
            {var subQ0=sQuery(id+"F14.wireOp",EDGE,"E81.bottom");var subQ1=sQuery(id+"F14.wireOp",EDGE,"E76.left");var subQ2=makeQuery(id+"F14.imprint","INTERSECT",VERTEX,{"derivedFrom":[subQ1,subQ0]});Q3=makeQuery(id+"F14.imprint","IMPRINT",FACE,{"disambiguationData":[TD([[makeQuery(id+"F14.imprint","IMPRINT",EDGE,{"disambiguationData":[TD([[subQ2,1.0]])],"derivedFrom":subQ1}),-1.0]])]});}
            var Q4;
            {var subQ0=sQuery(id+"F14.wireOp",EDGE,"E81.bottom");var subQ1=sQuery(id+"F14.wireOp",EDGE,"E76.right");var subQ2=makeQuery(id+"F14.imprint","INTERSECT",VERTEX,{"derivedFrom":[subQ1,subQ0]});Q4=makeQuery(id+"F14.imprint","IMPRINT",FACE,{"disambiguationData":[TD([[makeQuery(id+"F14.imprint","IMPRINT",EDGE,{"disambiguationData":[TD([[subQ2,1.0]])],"derivedFrom":subQ1}),1.0]])]});}
            var Q5;
            {var subQ0=sQuery(id+"F14.wireOp",EDGE,"E82.left");var subQ1=sQuery(id+"F14.wireOp",EDGE,"E77.bottom");var subQ2=makeQuery(id+"F14.imprint","INTERSECT",VERTEX,{"derivedFrom":[subQ1,subQ0]});Q5=makeQuery(id+"F14.imprint","IMPRINT",FACE,{"disambiguationData":[TD([[makeQuery(id+"F14.imprint","IMPRINT",EDGE,{"disambiguationData":[TD([[subQ2,1.0]])],"derivedFrom":subQ1}),-1.0]])]});}
            var Q6;
            {var subQ2=sQuery(id+"F14.wireOp",EDGE,"E78.left");Q6=makeQuery(id+"F14.imprint","IMPRINT",FACE,{"disambiguationData":[TD([[makeQuery(id+"F14.imprint","IMPRINT",EDGE,{"derivedFrom":subQ2}),-1.0]])]});}
            var Q7;
            {var subQ2=sQuery(id+"F14.wireOp",EDGE,"E79.right");Q7=makeQuery(id+"F14.imprint","IMPRINT",FACE,{"disambiguationData":[TD([[makeQuery(id+"F14.imprint","IMPRINT",EDGE,{"derivedFrom":subQ2}),1.0]])]});}
            var Q8;
            {var subQ1=sQuery(id+"F14.wireOp",EDGE,"E80.bottom");Q8=makeQuery(id+"F14.imprint","IMPRINT",FACE,{"disambiguationData":[TD([[makeQuery(id+"F14.imprint","IMPRINT",EDGE,{"derivedFrom":subQ1}),1.0]])]});}
            var Q9;
            {var subQ0=sQuery(id+"F14.wireOp",EDGE,"E82.left");var subQ1=sQuery(id+"F14.wireOp",EDGE,"E81.bottom");var subQ2=makeQuery(id+"F14.imprint","INTERSECT",VERTEX,{"derivedFrom":[subQ1,subQ0]});Q9=makeQuery(id+"F14.imprint","IMPRINT",FACE,{"disambiguationData":[TD([[makeQuery(id+"F14.imprint","IMPRINT",EDGE,{"disambiguationData":[TD([[subQ2,1.0]])],"derivedFrom":subQ1}),-1.0]])]});}
            var Q10;
            {var subQ6=sQuery(id+"F14.wireOp",EDGE,"E78.top");Q10=makeQuery(id+"F14.imprint","IMPRINT",FACE,{"disambiguationData":[TD([[makeQuery(id+"F14.imprint","IMPRINT",EDGE,{"derivedFrom":subQ6}),-1.0]])]});}
            var Q11;
            {var subQ12=sQuery(id+"F14.wireOp",EDGE,"E76.bottom");Q11=makeQuery(id+"F14.imprint","IMPRINT",FACE,{"disambiguationData":[TD([[makeQuery(id+"F14.imprint","IMPRINT",EDGE,{"derivedFrom":subQ12}),1.0]])]});}
            extrude(context, id + "F15", {"entities" : qUnion([Q0, Q1, Q2, Q3, Q4, Q5, Q6, Q7, Q8, Q9, Q10, Q11]), "depth" : 3500 * mm, "offsetDistance" : 25 * mm});
        }
        {
            var Q0;
            Q0=qCreatedBy(makeId("Top.planeOp"),FACE);
            var sketch = newSketch(context, id + "F16", { "sketchPlane" : qUnion([Q0])});
            skLineSegment(sketch, "E83.bottom", {"start": v(14340.9, 21215.5) * mm, "end": v(22412.33, 21215.5) * mm});
            skLineSegment(sketch, "E83.top", {"start": v(14340.9, 30094.6) * mm, "end": v(22412.33, 30094.6) * mm});
            skLineSegment(sketch, "E83.left", {"start": v(14340.9, 21215.5) * mm, "end": v(14340.9, 30094.6) * mm});
            skLineSegment(sketch, "E83.right", {"start": v(22412.33, 21215.5) * mm, "end": v(22412.33, 30094.6) * mm});
            skLineSegment(sketch, "E84.bottom", {"start": v(14538.95, 29865.03) * mm, "end": v(19536.23, 29865.03) * mm});
            skLineSegment(sketch, "E84.top", {"start": v(14538.95, 27177.18) * mm, "end": v(19536.23, 27177.18) * mm});
            skLineSegment(sketch, "E84.left", {"start": v(14538.95, 29865.03) * mm, "end": v(14538.95, 27177.18) * mm});
            skLineSegment(sketch, "E84.right", {"start": v(19536.23, 29865.03) * mm, "end": v(19536.23, 27177.18) * mm});
            skLineSegment(sketch, "E85.bottom", {"start": v(14538.95, 26978.05) * mm, "end": v(19515.96, 26978.05) * mm});
            skLineSegment(sketch, "E85.top", {"start": v(14538.95, 21379.6) * mm, "end": v(19515.96, 21379.6) * mm});
            skLineSegment(sketch, "E85.left", {"start": v(14538.95, 26978.05) * mm, "end": v(14538.95, 21379.6) * mm});
            skLineSegment(sketch, "E85.right", {"start": v(19515.96, 26978.05) * mm, "end": v(19515.96, 21379.6) * mm});
            skLineSegment(sketch, "E86.bottom", {"start": v(19714.7, 21379.6) * mm, "end": v(22215.02, 21379.6) * mm});
            skLineSegment(sketch, "E86.top", {"start": v(19714.7, 26978.05) * mm, "end": v(22215.02, 26978.05) * mm});
            skLineSegment(sketch, "E86.left", {"start": v(19714.7, 21379.6) * mm, "end": v(19714.7, 26978.05) * mm});
            skLineSegment(sketch, "E86.right", {"start": v(22215.02, 21379.6) * mm, "end": v(22215.02, 26978.05) * mm});
            skLineSegment(sketch, "E87.bottom", {"start": v(19714.7, 27177.18) * mm, "end": v(22196.24, 27177.18) * mm});
            skLineSegment(sketch, "E87.top", {"start": v(19714.7, 29865.03) * mm, "end": v(22196.24, 29865.03) * mm});
            skLineSegment(sketch, "E87.left", {"start": v(19714.7, 27177.18) * mm, "end": v(19714.7, 29865.03) * mm});
            skLineSegment(sketch, "E87.right", {"start": v(22196.24, 27177.18) * mm, "end": v(22196.24, 29865.03) * mm});
            skSolve(sketch);
        }
        {
            var Q0;
            Q0=makeQuery(id+"F16.imprint","IMPRINT",FACE,{"disambiguationData":[TD([[makeQuery(id+"F16.imprint","IMPRINT",EDGE,{"derivedFrom":sQuery(id+"F16.wireOp",EDGE,"E83.bottom")}),1.0]])]});
            extrude(context, id + "F17", {"entities" : qUnion([Q0]), "depth" : 3500 * mm, "offsetDistance" : 25 * mm});
        }
        {
            var Q0;
            Q0=qCreatedBy(makeId("Top.planeOp"),FACE);
            var sketch = newSketch(context, id + "F18", { "sketchPlane" : qUnion([Q0])});
            skLineSegment(sketch, "E88.bottom", {"start": v(6074.85, 31057.15) * mm, "end": v(7240.72, 31057.15) * mm});
            skLineSegment(sketch, "E88.top", {"start": v(6074.85, 33596.2) * mm, "end": v(7240.72, 33596.2) * mm});
            skLineSegment(sketch, "E88.left", {"start": v(6074.85, 31057.15) * mm, "end": v(6074.85, 33596.2) * mm});
            skLineSegment(sketch, "E88.right", {"start": v(7240.72, 31057.15) * mm, "end": v(7240.72, 33596.2) * mm});
            skLineSegment(sketch, "E89.bottom", {"start": v(6175.43, 31162.25) * mm, "end": v(7134.98, 31162.25) * mm});
            skLineSegment(sketch, "E89.top", {"start": v(6175.43, 32202.8) * mm, "end": v(7134.98, 32202.8) * mm});
            skLineSegment(sketch, "E89.left", {"start": v(6175.43, 31162.25) * mm, "end": v(6175.43, 32202.8) * mm});
            skLineSegment(sketch, "E89.right", {"start": v(7134.98, 31162.25) * mm, "end": v(7134.98, 32202.8) * mm});
            skLineSegment(sketch, "E90.bottom", {"start": v(6175.43, 32489.43) * mm, "end": v(7134.98, 32489.43) * mm});
            skLineSegment(sketch, "E90.top", {"start": v(6175.43, 33498.83) * mm, "end": v(7134.98, 33498.83) * mm});
            skLineSegment(sketch, "E90.left", {"start": v(6175.43, 32489.43) * mm, "end": v(6175.43, 33498.83) * mm});
            skLineSegment(sketch, "E90.right", {"start": v(7134.98, 32489.43) * mm, "end": v(7134.98, 33498.83) * mm});
            skSolve(sketch);
        }
        {
            var Q0;
            Q0=qCreatedBy(makeId("Top.planeOp"),FACE);
            var sketch = newSketch(context, id + "F19", { "sketchPlane" : qUnion([Q0])});
            skLineSegment(sketch, "E91.bottom", {"start": v(16277.1, 32864.72) * mm, "end": v(20207.16, 32864.72) * mm});
            skLineSegment(sketch, "E91.top", {"start": v(16277.1, 31446.03) * mm, "end": v(20207.16, 31446.03) * mm});
            skLineSegment(sketch, "E91.left", {"start": v(16277.1, 32864.72) * mm, "end": v(16277.1, 31446.03) * mm});
            skLineSegment(sketch, "E91.right", {"start": v(20207.16, 32864.72) * mm, "end": v(20207.16, 31446.03) * mm});
            skLineSegment(sketch, "E92.top", {"start": v(16277.1, 32424.13) * mm, "end": v(20207.16, 32424.13) * mm});
            skLineSegment(sketch, "E92.left", {"start": v(16277.1, 32864.72) * mm, "end": v(16277.1, 32424.13) * mm});
            skLineSegment(sketch, "E92.right", {"start": v(20207.16, 32864.72) * mm, "end": v(20207.16, 32424.13) * mm});
            skLineSegment(sketch, "E93.top", {"start": v(16277.1, 31948.3) * mm, "end": v(20207.16, 31948.3) * mm});
            skLineSegment(sketch, "E93.left", {"start": v(16277.1, 31446.03) * mm, "end": v(16277.1, 31948.3) * mm});
            skLineSegment(sketch, "E93.right", {"start": v(20207.16, 31446.03) * mm, "end": v(20207.16, 31948.3) * mm});
            skSolve(sketch);
        }
        {
            var Q0;
            {var subQ0=sQuery(id+"F19.wireOp",EDGE,"E91.top");Q0=makeQuery(id+"F19.imprint","IMPRINT",FACE,{"disambiguationData":[TD([[makeQuery(id+"F19.imprint","IMPRINT",EDGE,{"derivedFrom":subQ0}),1.0]])]});}
            var Q1;
            {var subQ0=sQuery(id+"F19.wireOp",EDGE,"E91.bottom");Q1=makeQuery(id+"F19.imprint","IMPRINT",FACE,{"disambiguationData":[TD([[makeQuery(id+"F19.imprint","IMPRINT",EDGE,{"derivedFrom":subQ0}),-1.0]])]});}
            extrude(context, id + "F20", {"entities" : qUnion([Q0, Q1]), "depth" : 750 * mm, "offsetDistance" : 25 * mm});
        }
        {
            var Q0;
            Q0=qCreatedBy(makeId("Top.planeOp"),FACE);
            var sketch = newSketch(context, id + "F21", { "sketchPlane" : qUnion([Q0])});
            skLineSegment(sketch, "E94.bottom", {"start": v(21431.07, 33048.27) * mm, "end": v(22752.01, 33048.27) * mm});
            skLineSegment(sketch, "E94.top", {"start": v(21431.07, 30992.08) * mm, "end": v(22752.01, 30992.08) * mm});
            skLineSegment(sketch, "E94.left", {"start": v(21431.07, 33048.27) * mm, "end": v(21431.07, 30992.08) * mm});
            skLineSegment(sketch, "E94.right", {"start": v(22752.01, 33048.27) * mm, "end": v(22752.01, 30992.08) * mm});
            skPoint(sketch, "E95.oppositeSnap0", {"position": v(22752.01, 32020.18) * mm});
            skLineSegment(sketch, "E95.bottom", {"start": v(22752.01, 30992.08) * mm, "end": v(23724.03, 30992.08) * mm});
            skLineSegment(sketch, "E95.top", {"start": v(22752.01, 32020.18) * mm, "end": v(23724.03, 32020.18) * mm});
            skLineSegment(sketch, "E95.left", {"start": v(22752.01, 30992.08) * mm, "end": v(22752.01, 32020.18) * mm});
            skLineSegment(sketch, "E95.right", {"start": v(23724.03, 30992.08) * mm, "end": v(23724.03, 32020.18) * mm});
            skSolve(sketch);
        }
        {
            var Q0;
            {var subQ3=sQuery(id+"F21.wireOp",EDGE,"E94.bottom");Q0=makeQuery(id+"F21.imprint","IMPRINT",FACE,{"disambiguationData":[TD([[makeQuery(id+"F21.imprint","IMPRINT",EDGE,{"derivedFrom":subQ3}),-1.0]])]});}
            var Q1;
            {var subQ0=sQuery(id+"F21.wireOp",EDGE,"E95.bottom");Q1=makeQuery(id+"F21.imprint","IMPRINT",FACE,{"disambiguationData":[TD([[makeQuery(id+"F21.imprint","IMPRINT",EDGE,{"derivedFrom":subQ0}),1.0]])]});}
            extrude(context, id + "F22", {"entities" : qUnion([Q0, Q1]), "depth" : 1500 * mm, "offsetDistance" : 25 * mm});
        }
        {
            var Q0;
            Q0=qCreatedBy(makeId("Top.planeOp"),FACE);
            var sketch = newSketch(context, id + "F23", { "sketchPlane" : qUnion([Q0])});
            skLineSegment(sketch, "E96.bottom", {"start": v(0, 0) * mm, "end": v(29984.63, 0) * mm});
            skLineSegment(sketch, "E96.top", {"start": v(0, 42429.96) * mm, "end": v(29984.63, 42429.96) * mm});
            skLineSegment(sketch, "E96.left", {"start": v(0, 0) * mm, "end": v(0, 42429.96) * mm});
            skLineSegment(sketch, "E96.right", {"start": v(29984.63, 0) * mm, "end": v(29984.63, 42429.96) * mm});
            skSolve(sketch);
        }
        {
            var Q0;
            Q0=makeQuery(id+"F23.imprint","IMPRINT",FACE,{"disambiguationData":[TD([[makeQuery(id+"F23.imprint","IMPRINT",EDGE,{"derivedFrom":sQuery(id+"F23.wireOp",EDGE,"E96.bottom")}),1.0]])]});
            extrude(context, id + "F24", {"entities" : qUnion([Q0]), "operationType" : NewBodyOperationType.ADD, "depth" : -250 * mm, "offsetDistance" : 25 * mm});
        }
        {
            var Q0;
            Q0=makeQuery(id+"F18.imprint","IMPRINT",FACE,{"disambiguationData":[TD([[makeQuery(id+"F18.imprint","IMPRINT",EDGE,{"derivedFrom":sQuery(id+"F18.wireOp",EDGE,"E88.bottom")}),1.0]])]});
            extrude(context, id + "F25", {"entities" : qUnion([Q0]), "depth" : 3000 * mm, "offsetDistance" : 25 * mm});
        }
    });
